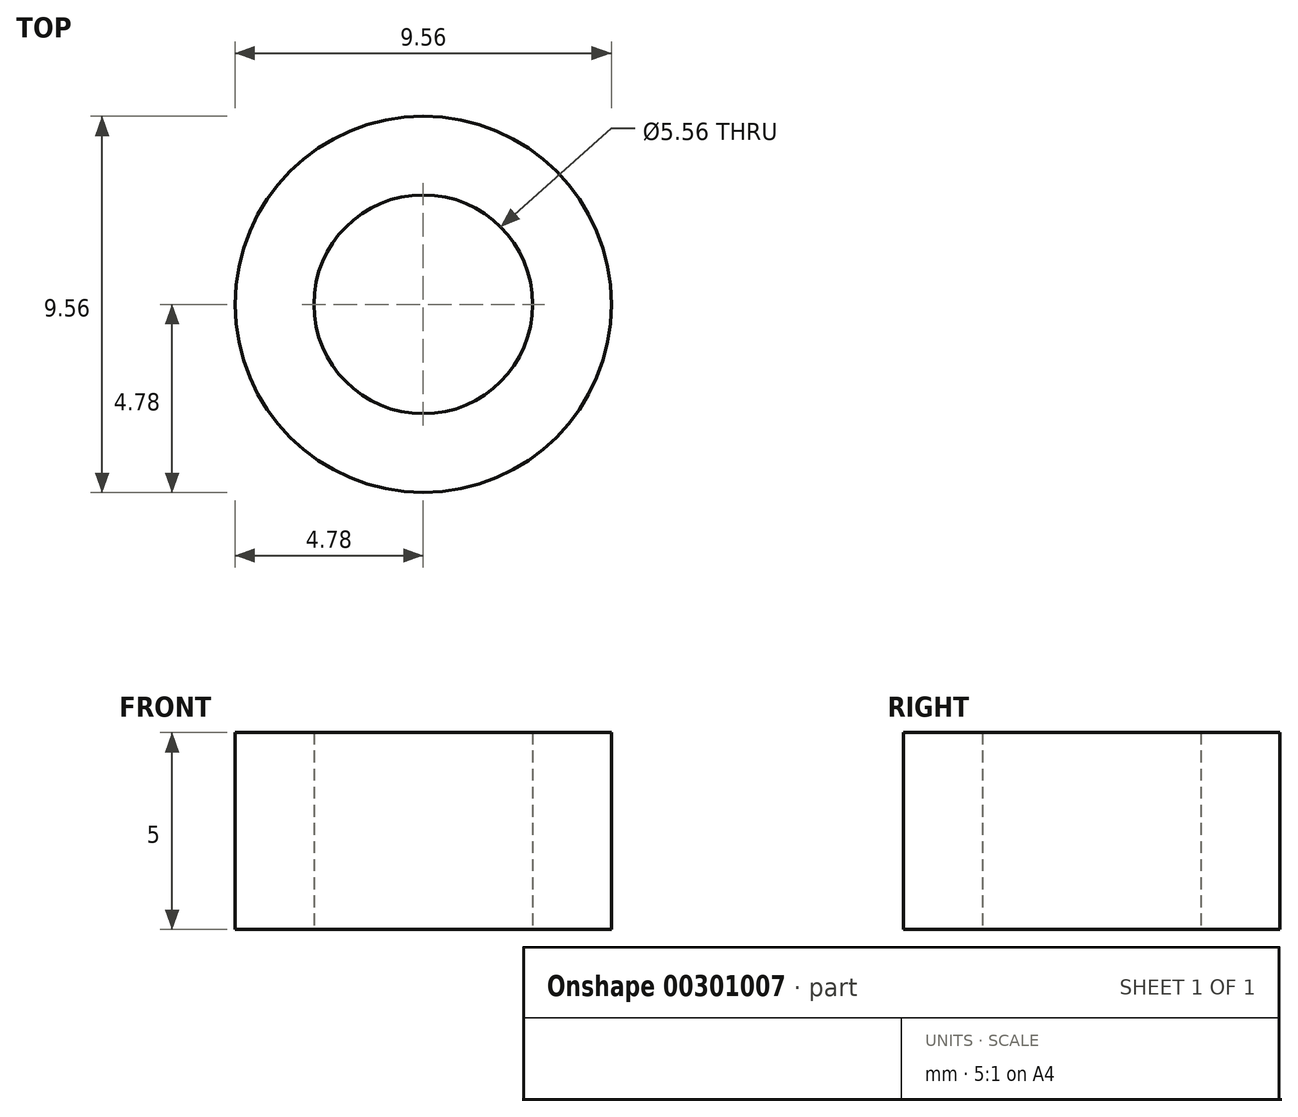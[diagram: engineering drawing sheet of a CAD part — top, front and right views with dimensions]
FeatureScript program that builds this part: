
annotation { "Feature Type Name" : "Feature", "Feature Type Description" : "" }
export const myFeature = defineFeature(function(context is Context, id is Id, definition is map)
    precondition{}
    {
        {
            var Q0;
            Q0=qCreatedBy(makeId("Top.planeOp"),FACE);
            var sketch = newSketch(context, id + "F0", { "sketchPlane" : qUnion([Q0])});
            skCircle(sketch, "E0", {"center": v(0, 0) * mm, "radius": 2.78 * mm});
            skCircle(sketch, "E1", {"center": v(0, 0) * mm, "radius": 4.78 * mm});
            skSolve(sketch);
        }
        {
            var Q0;
            Q0=makeQuery(id+"F0.imprint","IMPRINT",FACE,{"disambiguationData":[TD([[makeQuery(id+"F0.imprint","IMPRINT",EDGE,{"derivedFrom":sQuery(id+"F0.wireOp",EDGE,"E0")}),-1.0]])]});
            extrude(context, id + "F1", {"entities" : qUnion([Q0]), "depth" : 5 * mm, "offsetDistance" : 25 * mm});
        }
    });
